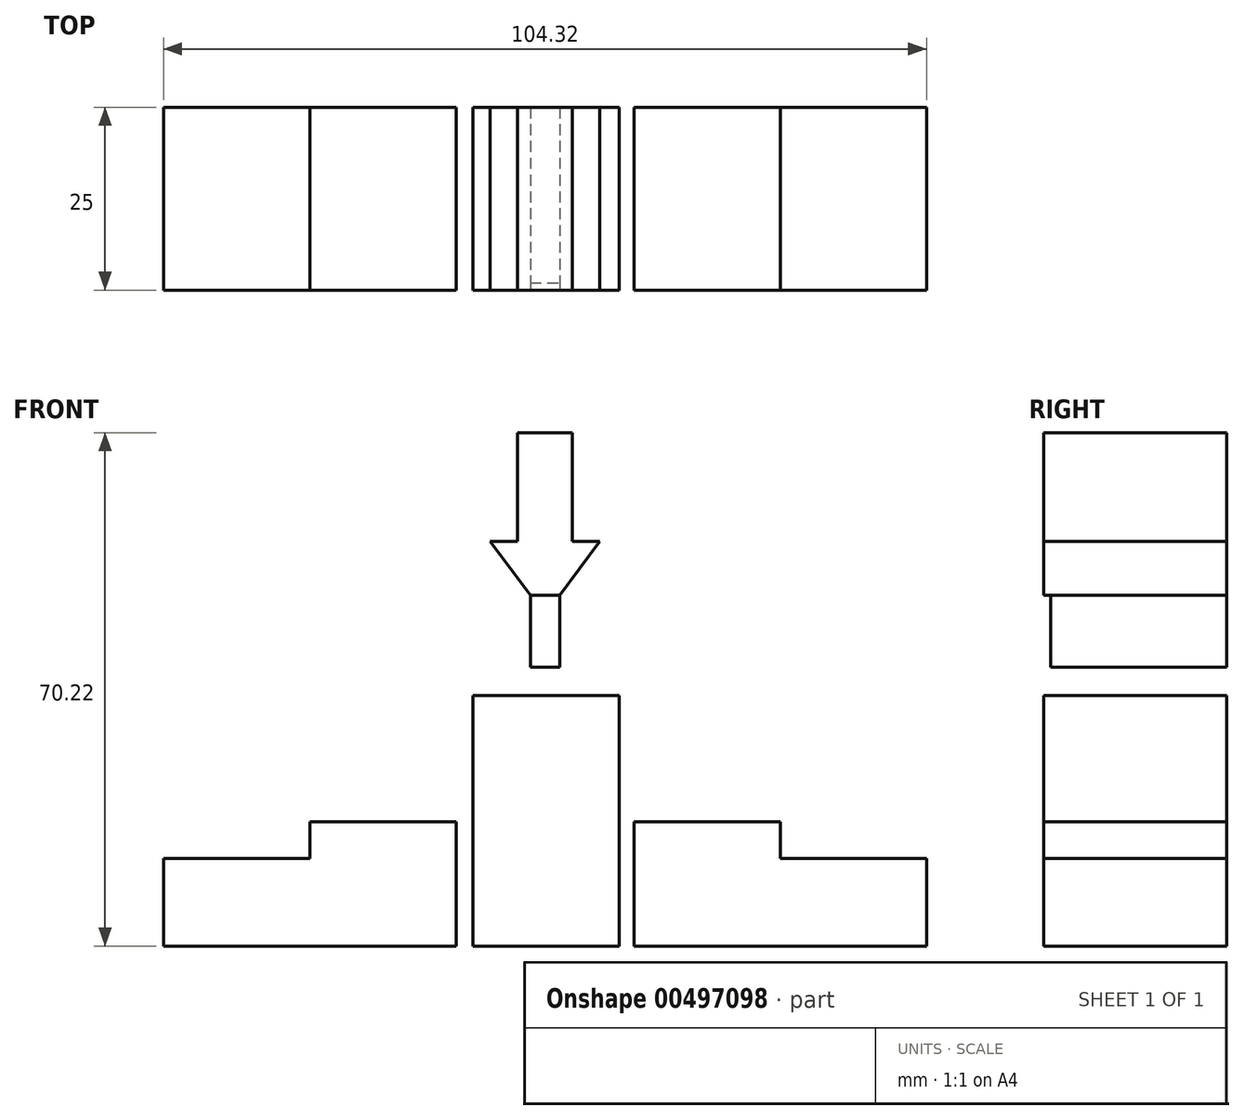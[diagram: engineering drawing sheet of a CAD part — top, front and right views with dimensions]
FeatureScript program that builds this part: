
annotation { "Feature Type Name" : "Feature", "Feature Type Description" : "" }
export const myFeature = defineFeature(function(context is Context, id is Id, definition is map)
    precondition{}
    {
        {
            var Q0;
            Q0=qCreatedBy(makeId("Front.planeOp"),FACE);
            var sketch = newSketch(context, id + "F0", { "sketchPlane" : qUnion([Q0])});
            skLineSegment(sketch, "E0.bottom", {"start": v(87.05, 42.95) * mm, "end": v(67.05, 42.95) * mm});
            skLineSegment(sketch, "E0.top", {"start": v(87.05, 8.66) * mm, "end": v(67.05, 8.66) * mm});
            skLineSegment(sketch, "E0.left", {"start": v(87.05, 42.95) * mm, "end": v(87.05, 8.66) * mm});
            skLineSegment(sketch, "E0.right", {"start": v(67.05, 42.95) * mm, "end": v(67.05, 8.66) * mm});
            skPoint(sketch, "E0.middle", {"position": v(77.05, 25.8) * mm});
            skLineSegment(sketch, "E1.bottom", {"start": v(89.05, 8.66) * mm, "end": v(129.05, 8.66) * mm});
            skLineSegment(sketch, "E1.top", {"start": v(89.05, 20.66) * mm, "end": v(129.05, 20.66) * mm});
            skLineSegment(sketch, "E1.left", {"start": v(89.05, 8.66) * mm, "end": v(89.05, 20.66) * mm});
            skLineSegment(sketch, "E1.right", {"start": v(129.05, 8.66) * mm, "end": v(129.05, 20.66) * mm});
            skLineSegment(sketch, "E2.bottom", {"start": v(89.05, 20.66) * mm, "end": v(109.05, 20.66) * mm});
            skLineSegment(sketch, "E2.top", {"start": v(89.05, 25.66) * mm, "end": v(109.05, 25.66) * mm});
            skLineSegment(sketch, "E2.left", {"start": v(89.05, 20.66) * mm, "end": v(89.05, 25.66) * mm});
            skLineSegment(sketch, "E2.right", {"start": v(109.05, 20.66) * mm, "end": v(109.05, 25.66) * mm});
            skLineSegment(sketch, "E3", {"start": v(76.89, 63.98) * mm, "end": v(76.89, 78.88) * mm, "construction": true});
            skPoint(sketch, "E3.startSnap0", {"position": v(77.05, 42.95) * mm});
            skLineSegment(sketch, "E4", {"start": v(84.39, 63.98) * mm, "end": v(78.89, 56.65) * mm});
            skLineSegment(sketch, "E5", {"start": v(84.39, 63.98) * mm, "end": v(76.89, 63.98) * mm});
            skLineSegment(sketch, "E6.MirrorCS", {"start": v(69.39, 63.98) * mm, "end": v(76.89, 63.98) * mm});
            skLineSegment(sketch, "E7.MirrorCS", {"start": v(69.39, 63.98) * mm, "end": v(74.89, 56.65) * mm});
            skLineSegment(sketch, "E8.bottom", {"start": v(80.64, 63.98) * mm, "end": v(73.14, 63.98) * mm});
            skLineSegment(sketch, "E8.top", {"start": v(80.64, 78.88) * mm, "end": v(73.14, 78.88) * mm});
            skLineSegment(sketch, "E8.left", {"start": v(80.64, 63.98) * mm, "end": v(80.64, 78.88) * mm});
            skLineSegment(sketch, "E8.right", {"start": v(73.14, 63.98) * mm, "end": v(73.14, 78.88) * mm});
            skPoint(sketch, "E8.middle", {"position": v(76.89, 71.43) * mm});
            skLineSegment(sketch, "E9.left", {"start": v(78.89, 51.15) * mm, "end": v(78.89, 58.82) * mm});
            skLineSegment(sketch, "E9.right", {"start": v(74.89, 51.15) * mm, "end": v(74.89, 58.82) * mm});
            skPoint(sketch, "E9.middle", {"position": v(76.89, 54.98) * mm});
            skLineSegment(sketch, "E10.top", {"start": v(74.89, 46.82) * mm, "end": v(78.89, 46.82) * mm});
            skLineSegment(sketch, "E10.left", {"start": v(74.89, 58.82) * mm, "end": v(74.89, 46.82) * mm});
            skLineSegment(sketch, "E10.right", {"start": v(78.89, 58.82) * mm, "end": v(78.89, 46.82) * mm});
            skLineSegment(sketch, "E11.MirrorCS", {"start": v(44.73, 20.66) * mm, "end": v(44.73, 25.66) * mm});
            skLineSegment(sketch, "E12.MirrorCS", {"start": v(64.73, 20.66) * mm, "end": v(64.73, 25.66) * mm});
            skLineSegment(sketch, "E13.MirrorCS", {"start": v(64.73, 25.66) * mm, "end": v(44.73, 25.66) * mm});
            skLineSegment(sketch, "E14.MirrorCS", {"start": v(64.73, 20.66) * mm, "end": v(44.73, 20.66) * mm});
            skLineSegment(sketch, "E15.MirrorCS", {"start": v(24.73, 8.66) * mm, "end": v(24.73, 20.66) * mm});
            skLineSegment(sketch, "E16.MirrorCS", {"start": v(64.73, 8.66) * mm, "end": v(64.73, 20.66) * mm});
            skLineSegment(sketch, "E17.MirrorCS", {"start": v(64.73, 20.66) * mm, "end": v(24.73, 20.66) * mm});
            skLineSegment(sketch, "E18.MirrorCS", {"start": v(64.73, 8.66) * mm, "end": v(24.73, 8.66) * mm});
            skPoint(sketch, "E19.orphan", {"position": v(76.89, 53.98) * mm});
            skLineSegment(sketch, "E20", {"start": v(74.89, 58.82) * mm, "end": v(78.89, 58.82) * mm, "construction": true});
            skLineSegment(sketch, "E21", {"start": v(74.89, 56.65) * mm, "end": v(78.89, 56.65) * mm});
            skSolve(sketch);
        }
        {
            var Q0;
            Q0 = qSketchRegion(id + "F0", true);
            extrude(context, id + "F1", {"entities" : qUnion([Q0]), "oppositeDirection" : true, "depth" : 25 * mm, "offsetDistance" : 25 * mm});
        }
        {
            var Q0;
            {var subQ1=sQuery(id+"F0.wireOp",EDGE,"E10.top");Q0=makeQuery(id+"F0.imprint","IMPRINT",FACE,{"disambiguationData":[TD([[makeQuery(id+"F0.imprint","IMPRINT",EDGE,{"derivedFrom":subQ1}),1.0]])]});}
            var Q1;
            Q1=makeQuery(id+"F0.imprint","IMPRINT",FACE,{"disambiguationData":[TD([[makeQuery(id+"F0.imprint","IMPRINT",EDGE,{"derivedFrom":sQuery(id+"F0.wireOp",EDGE,"E8.bottom")}),-1.0]])]});
            extrude(context, id + "F2", {"entities" : qUnion([Q0, Q1]), "operationType" : NewBodyOperationType.REMOVE, "oppositeDirection" : true, "depth" : 1 * mm, "offsetDistance" : 25 * mm});
        }
    });
